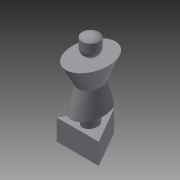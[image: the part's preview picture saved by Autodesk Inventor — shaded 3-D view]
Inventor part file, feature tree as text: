
AUTODESK INVENTOR PART (.ipt)
format: ipt  version: 2015 (Build 190159000, 159)  size: 250,368 bytes
history: native  units: in
note: dims shown in document units (in); Inventor stores cm internally (conversion verified against a paired STEP export)
features: sketch x8, plane x4, loft x3, extrude x1, revolve x1, projected_geometry x1, other x1
ambient origin geometry x8: Origin, YZ Plane, XZ Plane, XY Plane, X Axis, Y Axis, Z Axis, Center Point
bodies: Solid1 (feature_tree)
feature tree (19):
  extrude  "Extrusion1"  TaperAngle=0.0deg  [1 undecoded]
  sketch  "Sketch2"  dims[d5=0.32in d6=0.0in d8=0.105in]
  plane  "Work Plane1"
  loft  "Loft1"
  plane  "Work Plane2"
  sketch  "Sketch4"  dims[d11=0.11in d12=0.14in]
  loft  "Loft2"
  plane  "Work Plane3"
  loft  "Loft3"
  sketch  "Sketch8"  dims[d17=0.0in d18=90.0deg]
  plane  "Work Plane4"
  revolve  "Revolution1"  [1 undecoded]
  sketch  "Sketch1"  dims[d1=0.556in d3=0.0in]
  projected_geometry  "Projected Loop1"
  sketch  "Sketch3"  dims[d9=0.125in d10=0.19in]
  sketch  "Sketch5"  dims[d13=0.0in d14=0.0in]
  sketch  "Sketch7"  dims[d15=0.0in d16=90.0deg]
  other  "Edges1"
  sketch  "Sketch9"  dims[d19=0.36in d20=0.155in d21=0.195in d22=0.2in d23=0.3in d24=0.0in d25=90.0deg d26=0.0in d27=90.0deg d28=0.34in d29=0.27in d30=0.38in d31=0.0in d32=90.0deg d33=0.0in d34=90.0deg d35=90.0deg d36=90.0deg]
note: 2 required parameter values undecoded (feature->parameter linkage not recoverable at this tier; creation-order binding heuristic only, values carry confidence <= 0.55)